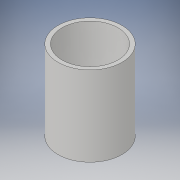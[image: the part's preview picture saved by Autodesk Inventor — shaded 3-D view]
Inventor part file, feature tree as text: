
AUTODESK INVENTOR PART (.ipt)
format: ipt  version: 2019.4 (Build 234330000, 330)  size: 95,232 bytes
history: native  units: mm
features: extrude x1, sketch x1
ambient origin geometry x8: Origin, YZ Plane, XZ Plane, XY Plane, X Axis, Y Axis, Z Axis, Center Point
bodies: Solid1 (feature_tree)
feature tree (2):
  extrude  "Extrusion1"  Depth=5.0mm
  sketch  "Sketch1"  dims[d0=3.5mm d1=4.0mm d2=5.0mm d3=0.0mm]
